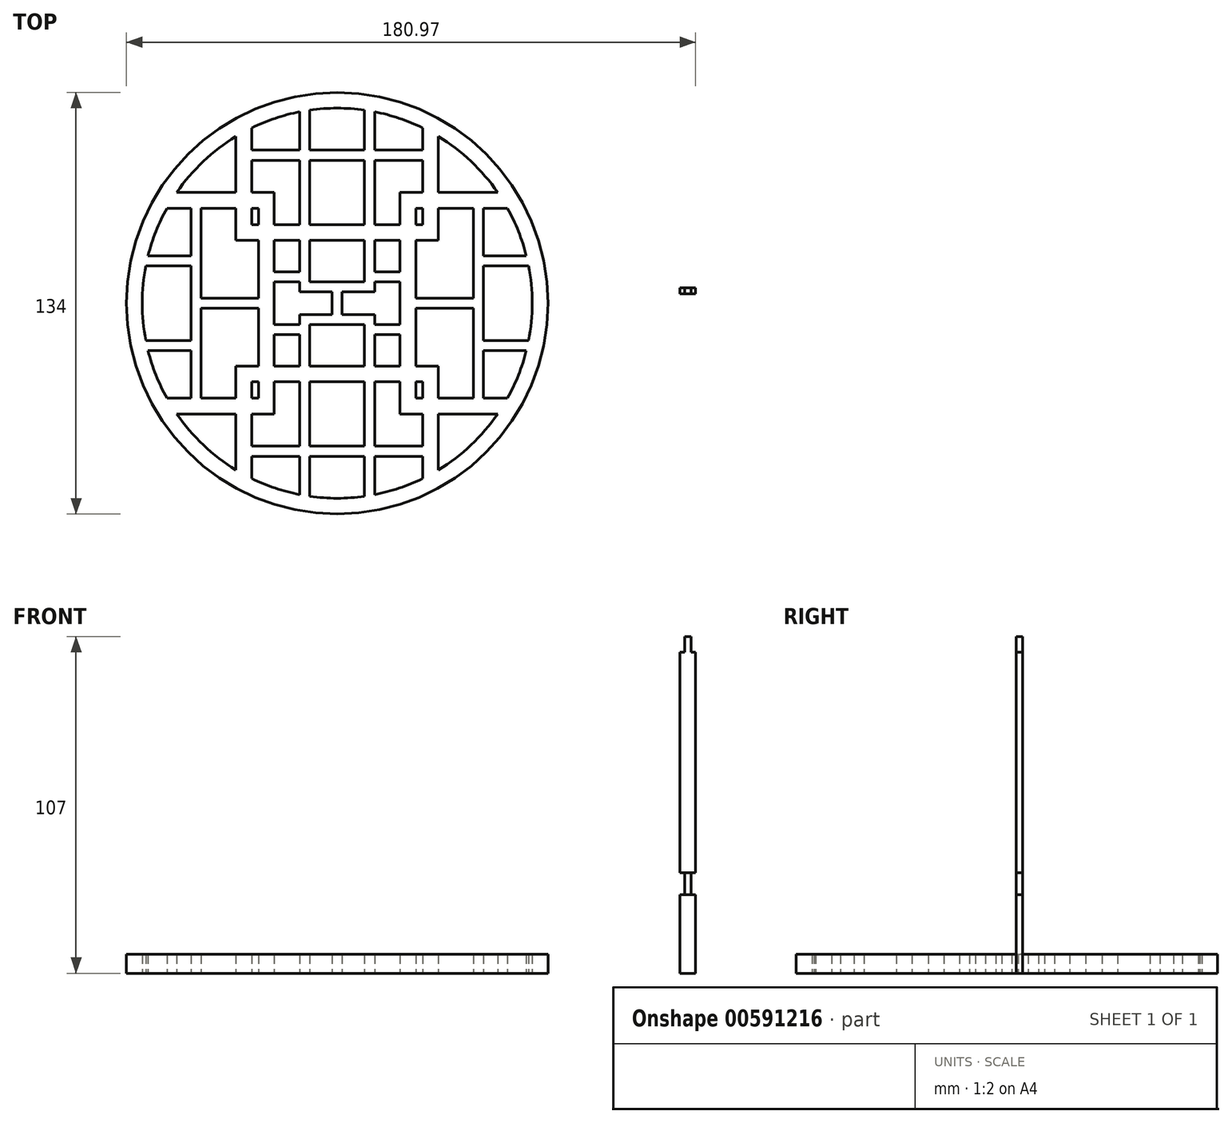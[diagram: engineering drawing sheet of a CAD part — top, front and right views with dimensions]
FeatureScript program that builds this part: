
annotation { "Feature Type Name" : "Feature", "Feature Type Description" : "" }
export const myFeature = defineFeature(function(context is Context, id is Id, definition is map)
    precondition{}
    {
        {
            var Q0;
            Q0=qCreatedBy(makeId("Top.planeOp"),FACE);
            var sketch = newSketch(context, id + "F0", { "sketchPlane" : qUnion([Q0])});
            skCircle(sketch, "E0", {"center": v(0, 0) * mm, "radius": 67 * mm});
            skArc(sketch, "E1.0", {"start": v(-54.15, 30.2) * mm, "mid": v(-57.64, 22.85) * mm, "end": v(-60.13, 15.1) * mm});
            skLineSegment(sketch, "E2.bottom", {"start": v(-27.2, 30.2) * mm, "end": v(-25, 30.2) * mm});
            skLineSegment(sketch, "E2.top", {"start": v(-27.2, 25) * mm, "end": v(-25, 25) * mm});
            skLineSegment(sketch, "E2.left", {"start": v(-27.2, 30.2) * mm, "end": v(-27.2, 25) * mm});
            skLineSegment(sketch, "E2.right", {"start": v(-25, 30.2) * mm, "end": v(-25, 25) * mm});
            skLineSegment(sketch, "E3.0", {"start": v(-20, 35.2) * mm, "end": v(-20, 25) * mm});
            skLineSegment(sketch, "E3.1", {"start": v(-27.2, 35.2) * mm, "end": v(-20, 35.2) * mm});
            skLineSegment(sketch, "E3.2", {"start": v(-32.2, 30.2) * mm, "end": v(-32.2, 20) * mm});
            skLineSegment(sketch, "E3.3", {"start": v(-32.2, 20) * mm, "end": v(-25, 20) * mm});
            skLineSegment(sketch, "E4", {"start": v(0, 62) * mm, "end": v(0, -62) * mm, "construction": true});
            skLineSegment(sketch, "E5", {"start": v(62, 0) * mm, "end": v(-62, 0) * mm, "construction": true});
            skLineSegment(sketch, "E6.0.1.0", {"start": v(-20, -25) * mm, "end": v(-20, -35.2) * mm});
            skLineSegment(sketch, "E6.0.1.1", {"start": v(-32.2, -20) * mm, "end": v(-32.2, -30.2) * mm});
            skLineSegment(sketch, "E6.0.1.2", {"start": v(-27.2, -35.2) * mm, "end": v(-20, -35.2) * mm});
            skLineSegment(sketch, "E6.0.1.3", {"start": v(-27.2, -30.2) * mm, "end": v(-25, -30.2) * mm});
            skLineSegment(sketch, "E6.0.1.4", {"start": v(-25, -25) * mm, "end": v(-25, -30.2) * mm});
            skLineSegment(sketch, "E6.0.1.5", {"start": v(-27.2, -25) * mm, "end": v(-27.2, -30.2) * mm});
            skLineSegment(sketch, "E6.0.1.6", {"start": v(-27.2, -25) * mm, "end": v(-25, -25) * mm});
            skLineSegment(sketch, "E6.0.1.7", {"start": v(-32.2, -20) * mm, "end": v(-25, -20) * mm});
            skLineSegment(sketch, "E6.1.0.0", {"start": v(32.2, 30.2) * mm, "end": v(32.2, 20) * mm});
            skLineSegment(sketch, "E6.1.0.1", {"start": v(20, 35.2) * mm, "end": v(20, 25) * mm});
            skLineSegment(sketch, "E6.1.0.2", {"start": v(25, 20) * mm, "end": v(32.2, 20) * mm});
            skLineSegment(sketch, "E6.1.0.3", {"start": v(25, 25) * mm, "end": v(27.2, 25) * mm});
            skLineSegment(sketch, "E6.1.0.4", {"start": v(27.2, 30.2) * mm, "end": v(27.2, 25) * mm});
            skLineSegment(sketch, "E6.1.0.5", {"start": v(25, 30.2) * mm, "end": v(25, 25) * mm});
            skLineSegment(sketch, "E6.1.0.6", {"start": v(25, 30.2) * mm, "end": v(27.2, 30.2) * mm});
            skLineSegment(sketch, "E6.1.0.7", {"start": v(20, 35.2) * mm, "end": v(27.2, 35.2) * mm});
            skLineSegment(sketch, "E6.1.1.0", {"start": v(32.2, -20) * mm, "end": v(32.2, -30.2) * mm});
            skLineSegment(sketch, "E6.1.1.1", {"start": v(20, -25) * mm, "end": v(20, -35.2) * mm});
            skLineSegment(sketch, "E6.1.1.2", {"start": v(20, -35.2) * mm, "end": v(27.2, -35.2) * mm});
            skLineSegment(sketch, "E6.1.1.3", {"start": v(25, -30.2) * mm, "end": v(27.2, -30.2) * mm});
            skLineSegment(sketch, "E6.1.1.4", {"start": v(27.2, -25) * mm, "end": v(27.2, -30.2) * mm});
            skLineSegment(sketch, "E6.1.1.5", {"start": v(25, -25) * mm, "end": v(25, -30.2) * mm});
            skLineSegment(sketch, "E6.1.1.6", {"start": v(25, -25) * mm, "end": v(27.2, -25) * mm});
            skLineSegment(sketch, "E6.1.1.7", {"start": v(25, -20) * mm, "end": v(32.2, -20) * mm});
            skLineSegment(sketch, "E6.direction1", {"start": v(-20, 20) * mm, "end": v(-11.9, 20) * mm, "construction": true});
            skLineSegment(sketch, "E6.direction2", {"start": v(-20, 20) * mm, "end": v(-20, 10) * mm, "construction": true});
            skLineSegment(sketch, "E7", {"start": v(-20, 20) * mm, "end": v(-20, 10) * mm});
            skLineSegment(sketch, "E8", {"start": v(-20, -20) * mm, "end": v(-11.9, -20) * mm});
            skLineSegment(sketch, "E9", {"start": v(20, 20) * mm, "end": v(20, 10) * mm});
            skLineSegment(sketch, "E10", {"start": v(20, 20) * mm, "end": v(11.9, 20) * mm});
            skLineSegment(sketch, "E11", {"start": v(25, 20) * mm, "end": v(25, 1.6) * mm});
            skPoint(sketch, "E12.orphan", {"position": v(-27.2, 20) * mm});
            skLineSegment(sketch, "E13", {"start": v(-25, 20) * mm, "end": v(-25, 1.6) * mm});
            skPoint(sketch, "E13.startSnap0", {"position": v(-26.1, 20) * mm});
            skLineSegment(sketch, "E14", {"start": v(-20, -25) * mm, "end": v(-11.9, -25) * mm});
            skLineSegment(sketch, "E15", {"start": v(20, 25) * mm, "end": v(11.9, 25) * mm});
            skLineSegment(sketch, "E16", {"start": v(27.2, -35.2) * mm, "end": v(27.2, -45.46) * mm});
            skPoint(sketch, "E16.startSnap0", {"position": v(26.1, -35.2) * mm});
            skLineSegment(sketch, "E17", {"start": v(32.2, -35.2) * mm, "end": v(32.2, -52.98) * mm});
            skLineSegment(sketch, "E18", {"start": v(32.2, -30.2) * mm, "end": v(43.26, -30.2) * mm});
            skPoint(sketch, "E18.startSnap0", {"position": v(32.2, -27.6) * mm});
            skLineSegment(sketch, "E19", {"start": v(32.2, -35.2) * mm, "end": v(51.04, -35.2) * mm});
            skLineSegment(sketch, "E20", {"start": v(32.2, 30.2) * mm, "end": v(43.26, 30.2) * mm});
            skLineSegment(sketch, "E21", {"start": v(32.2, 35.2) * mm, "end": v(51.04, 35.2) * mm});
            skLineSegment(sketch, "E22", {"start": v(32.2, 35.2) * mm, "end": v(32.2, 52.98) * mm});
            skLineSegment(sketch, "E23", {"start": v(27.2, 35.2) * mm, "end": v(27.2, 45.46) * mm});
            skLineSegment(sketch, "E24", {"start": v(-27.2, 35.2) * mm, "end": v(-27.2, 55.71) * mm});
            skLineSegment(sketch, "E25", {"start": v(-32.2, 35.2) * mm, "end": v(-32.2, 52.98) * mm});
            skLineSegment(sketch, "E26", {"start": v(-32.2, 35.2) * mm, "end": v(-51.04, 35.2) * mm});
            skLineSegment(sketch, "E27", {"start": v(-32.2, 30.2) * mm, "end": v(-43.26, 30.2) * mm});
            skLineSegment(sketch, "E28", {"start": v(-27.2, -35.2) * mm, "end": v(-27.2, -45.46) * mm});
            skPoint(sketch, "E28.startSnap0", {"position": v(-26.1, -35.2) * mm});
            skLineSegment(sketch, "E29", {"start": v(-32.2, -35.2) * mm, "end": v(-32.2, -52.98) * mm});
            skLineSegment(sketch, "E30", {"start": v(-32.2, -35.2) * mm, "end": v(-51.04, -35.2) * mm});
            skLineSegment(sketch, "E31", {"start": v(-32.2, -30.2) * mm, "end": v(-43.26, -30.2) * mm});
            skLineSegment(sketch, "E32", {"start": v(-11.9, -20) * mm, "end": v(-11.9, -10) * mm});
            skLineSegment(sketch, "E33.0", {"start": v(-8.7, -20) * mm, "end": v(-8.7, -6.8) * mm});
            skLineSegment(sketch, "E34", {"start": v(-11.9, -10) * mm, "end": v(-20, -10) * mm});
            skLineSegment(sketch, "E35", {"start": v(-11.9, -6.8) * mm, "end": v(-20, -6.8) * mm});
            skPoint(sketch, "E36.orphan", {"position": v(-11.9, 0) * mm});
            skLineSegment(sketch, "E37.trimOffspring", {"start": v(-20, -10) * mm, "end": v(-20, -20) * mm, "construction": true});
            skLineSegment(sketch, "E38.trimOffspring", {"start": v(-8.7, -20) * mm, "end": v(8.7, -20) * mm});
            skLineSegment(sketch, "E39.trimOffspring", {"start": v(-20, -25) * mm, "end": v(-20, -35.2) * mm, "construction": true});
            skLineSegment(sketch, "E40", {"start": v(-8.7, -6.8) * mm, "end": v(0, -6.8) * mm});
            skLineSegment(sketch, "E41", {"start": v(-1.6, -3.6) * mm, "end": v(-11.92, -3.6) * mm});
            skLineSegment(sketch, "E42", {"start": v(-11.92, -3.6) * mm, "end": v(-11.9, -6.8) * mm});
            skLineSegment(sketch, "E43", {"start": v(-1.6, -3.6) * mm, "end": v(-1.6, 0) * mm});
            skLineSegment(sketch, "E44.MirrorCS", {"start": v(8.7, -6.8) * mm, "end": v(0, -6.8) * mm});
            skLineSegment(sketch, "E45.MirrorCS", {"start": v(8.7, -20) * mm, "end": v(8.7, -6.8) * mm});
            skLineSegment(sketch, "E46.MirrorCS", {"start": v(11.9, -20) * mm, "end": v(11.9, -10) * mm});
            skLineSegment(sketch, "E47.MirrorCS", {"start": v(11.9, -10) * mm, "end": v(20, -10) * mm});
            skLineSegment(sketch, "E48.MirrorCS", {"start": v(11.9, -6.8) * mm, "end": v(20, -6.8) * mm});
            skLineSegment(sketch, "E49.MirrorCS", {"start": v(1.6, -3.6) * mm, "end": v(11.92, -3.6) * mm});
            skLineSegment(sketch, "E50.MirrorCS", {"start": v(1.6, -3.6) * mm, "end": v(1.6, 0) * mm});
            skLineSegment(sketch, "E51", {"start": v(11.92, -3.6) * mm, "end": v(11.9, -6.8) * mm});
            skLineSegment(sketch, "E52.MirrorCS", {"start": v(11.9, 10) * mm, "end": v(20, 10) * mm});
            skLineSegment(sketch, "E53.MirrorCS", {"start": v(11.9, 6.8) * mm, "end": v(20, 6.8) * mm});
            skLineSegment(sketch, "E54.MirrorCS", {"start": v(11.92, 3.6) * mm, "end": v(11.9, 6.8) * mm});
            skLineSegment(sketch, "E55.MirrorCS", {"start": v(1.6, 3.6) * mm, "end": v(11.92, 3.6) * mm});
            skLineSegment(sketch, "E56.MirrorCS", {"start": v(1.6, 3.6) * mm, "end": v(1.6, 0) * mm});
            skLineSegment(sketch, "E57.MirrorCS", {"start": v(-1.6, 3.6) * mm, "end": v(-1.6, 0) * mm});
            skLineSegment(sketch, "E58.MirrorCS", {"start": v(-8.7, 6.8) * mm, "end": v(0, 6.8) * mm});
            skLineSegment(sketch, "E59.MirrorCS", {"start": v(8.7, 6.8) * mm, "end": v(0, 6.8) * mm});
            skLineSegment(sketch, "E60.MirrorCS", {"start": v(8.7, 20) * mm, "end": v(8.7, 6.8) * mm});
            skLineSegment(sketch, "E61.MirrorCS", {"start": v(11.9, 20) * mm, "end": v(11.9, 10) * mm});
            skLineSegment(sketch, "E62.MirrorCS", {"start": v(-1.6, 3.6) * mm, "end": v(-11.92, 3.6) * mm});
            skLineSegment(sketch, "E63.MirrorCS", {"start": v(-8.7, 20) * mm, "end": v(-8.7, 6.8) * mm});
            skLineSegment(sketch, "E64.MirrorCS", {"start": v(-11.9, 20) * mm, "end": v(-11.9, 10) * mm});
            skLineSegment(sketch, "E65.MirrorCS", {"start": v(-11.9, 10) * mm, "end": v(-20, 10) * mm});
            skLineSegment(sketch, "E66.MirrorCS", {"start": v(-11.9, 6.8) * mm, "end": v(-20, 6.8) * mm});
            skLineSegment(sketch, "E67.MirrorCS", {"start": v(-11.92, 3.6) * mm, "end": v(-11.9, 6.8) * mm});
            skLineSegment(sketch, "E68.trimOffspring", {"start": v(-8.7, 20) * mm, "end": v(8.7, 20) * mm, "construction": true});
            skLineSegment(sketch, "E69.trimOffspring", {"start": v(-20, 6.8) * mm, "end": v(-20, -6.8) * mm, "construction": true});
            skLineSegment(sketch, "E70.trimOffspring", {"start": v(-20, 6.8) * mm, "end": v(-20, -6.8) * mm});
            skLineSegment(sketch, "E71.trimOffspring", {"start": v(-11.9, 20) * mm, "end": v(-20, 20) * mm});
            skLineSegment(sketch, "E72.trimOffspring", {"start": v(-20, -10) * mm, "end": v(-20, -20) * mm});
            skLineSegment(sketch, "E73.trimOffspring", {"start": v(11.9, -20) * mm, "end": v(20, -20) * mm});
            skLineSegment(sketch, "E74.trimOffspring", {"start": v(20, -10) * mm, "end": v(20, -20) * mm});
            skLineSegment(sketch, "E75.trimOffspring", {"start": v(20, 6.8) * mm, "end": v(20, -6.8) * mm});
            skLineSegment(sketch, "E76.trimOffspring", {"start": v(25, 20) * mm, "end": v(32.2, 20) * mm, "construction": true});
            skLineSegment(sketch, "E77.trimOffspring", {"start": v(11.9, 20) * mm, "end": v(20, 20) * mm, "construction": true});
            skLineSegment(sketch, "E78.trimOffspring", {"start": v(8.7, 20) * mm, "end": v(-8.7, 20) * mm});
            skArc(sketch, "E79.trimOffspring", {"start": v(-32.2, 52.98) * mm, "mid": v(-42.56, 45.09) * mm, "end": v(-51.04, 35.2) * mm});
            skArc(sketch, "E80.trimOffspring", {"start": v(27.2, 55.71) * mm, "mid": v(19.72, 58.78) * mm, "end": v(11.9, 60.85) * mm});
            skArc(sketch, "E81.trimOffspring", {"start": v(51.04, 35.2) * mm, "mid": v(42.56, 45.09) * mm, "end": v(32.2, 52.98) * mm});
            skArc(sketch, "E82.trimOffspring", {"start": v(54.15, -30.2) * mm, "mid": v(57.64, -22.85) * mm, "end": v(60.13, -15.1) * mm});
            skArc(sketch, "E83.trimOffspring", {"start": v(32.2, -52.98) * mm, "mid": v(42.56, -45.09) * mm, "end": v(51.04, -35.2) * mm});
            skArc(sketch, "E84.trimOffspring", {"start": v(-27.2, -55.71) * mm, "mid": v(-19.72, -58.78) * mm, "end": v(-11.9, -60.85) * mm});
            skArc(sketch, "E85.trimOffspring", {"start": v(-51.04, -35.2) * mm, "mid": v(-42.56, -45.09) * mm, "end": v(-32.2, -52.98) * mm});
            skLineSegment(sketch, "E86", {"start": v(-46.46, -30.2) * mm, "end": v(-46.46, -15.1) * mm});
            skLineSegment(sketch, "E87", {"start": v(-43.26, -30.2) * mm, "end": v(-43.26, -1.6) * mm});
            skLineSegment(sketch, "E88", {"start": v(-43.26, -1.6) * mm, "end": v(-25, -1.6) * mm});
            skPoint(sketch, "E89.orphan", {"position": v(-43.26, 0) * mm});
            skLineSegment(sketch, "E90", {"start": v(-46.46, -15.1) * mm, "end": v(-60.13, -15.1) * mm});
            skLineSegment(sketch, "E91", {"start": v(-46.46, -11.9) * mm, "end": v(-60.85, -11.9) * mm});
            skLineSegment(sketch, "E92.trimOffspring", {"start": v(-46.46, -11.9) * mm, "end": v(-46.46, 0) * mm});
            skArc(sketch, "E93.trimOffspring", {"start": v(-60.13, -15.1) * mm, "mid": v(-57.64, -22.85) * mm, "end": v(-54.15, -30.2) * mm});
            skLineSegment(sketch, "E94.MirrorCS", {"start": v(-43.26, 1.6) * mm, "end": v(-25, 1.6) * mm});
            skLineSegment(sketch, "E95.MirrorCS", {"start": v(-43.26, 30.2) * mm, "end": v(-43.26, 1.6) * mm});
            skLineSegment(sketch, "E96.MirrorCS", {"start": v(-46.46, 30.2) * mm, "end": v(-46.46, 15.1) * mm});
            skLineSegment(sketch, "E97.MirrorCS", {"start": v(-46.46, 11.9) * mm, "end": v(-46.46, 0) * mm});
            skLineSegment(sketch, "E98.MirrorCS", {"start": v(-46.46, 11.9) * mm, "end": v(-60.85, 11.9) * mm});
            skLineSegment(sketch, "E99.MirrorCS", {"start": v(-46.46, 15.1) * mm, "end": v(-60.13, 15.1) * mm});
            skLineSegment(sketch, "E100.MirrorCS", {"start": v(43.26, -30.2) * mm, "end": v(43.26, -1.6) * mm});
            skLineSegment(sketch, "E101.MirrorCS", {"start": v(43.26, -1.6) * mm, "end": v(25, -1.6) * mm});
            skLineSegment(sketch, "E102.MirrorCS", {"start": v(43.26, 1.6) * mm, "end": v(25, 1.6) * mm});
            skLineSegment(sketch, "E103.MirrorCS", {"start": v(46.46, -30.2) * mm, "end": v(46.46, -15.1) * mm});
            skLineSegment(sketch, "E104.MirrorCS", {"start": v(46.46, -11.9) * mm, "end": v(60.85, -11.9) * mm});
            skLineSegment(sketch, "E105.MirrorCS", {"start": v(46.46, 11.9) * mm, "end": v(60.85, 11.9) * mm});
            skLineSegment(sketch, "E106.MirrorCS", {"start": v(46.46, 15.1) * mm, "end": v(60.13, 15.1) * mm});
            skLineSegment(sketch, "E107.MirrorCS", {"start": v(43.26, 30.2) * mm, "end": v(43.26, 1.6) * mm});
            skLineSegment(sketch, "E108.MirrorCS", {"start": v(46.46, -15.1) * mm, "end": v(60.13, -15.1) * mm});
            skLineSegment(sketch, "E109.MirrorCS", {"start": v(46.46, 11.9) * mm, "end": v(46.46, 0) * mm});
            skLineSegment(sketch, "E110.MirrorCS", {"start": v(46.46, -11.9) * mm, "end": v(46.46, 0) * mm});
            skLineSegment(sketch, "E111.MirrorCS", {"start": v(46.46, 30.2) * mm, "end": v(46.46, 15.1) * mm});
            skLineSegment(sketch, "E112.trimOffspring", {"start": v(46.46, -30.2) * mm, "end": v(54.15, -30.2) * mm});
            skArc(sketch, "E113.trimOffspring", {"start": v(60.85, -11.9) * mm, "mid": v(62, 0) * mm, "end": v(60.85, 11.9) * mm});
            skArc(sketch, "E114.trimOffspring", {"start": v(60.13, 15.1) * mm, "mid": v(57.64, 22.85) * mm, "end": v(54.15, 30.2) * mm});
            skLineSegment(sketch, "E115.trimOffspring", {"start": v(46.46, 30.2) * mm, "end": v(54.15, 30.2) * mm});
            skLineSegment(sketch, "E116.trimOffspring", {"start": v(25, -1.6) * mm, "end": v(25, -20) * mm});
            skLineSegment(sketch, "E117.trimOffspring", {"start": v(-25, -1.6) * mm, "end": v(-25, -20) * mm});
            skArc(sketch, "E118.trimOffspring", {"start": v(-60.85, 11.9) * mm, "mid": v(-62, 0) * mm, "end": v(-60.85, -11.9) * mm});
            skLineSegment(sketch, "E119.trimOffspring", {"start": v(-46.46, -30.2) * mm, "end": v(-54.15, -30.2) * mm});
            skLineSegment(sketch, "E120.trimOffspring", {"start": v(-46.46, 30.2) * mm, "end": v(-54.15, 30.2) * mm});
            skLineSegment(sketch, "E121", {"start": v(-27.2, -45.46) * mm, "end": v(-11.9, -45.46) * mm});
            skLineSegment(sketch, "E122", {"start": v(-8.7, -25) * mm, "end": v(-8.7, -45.46) * mm});
            skPoint(sketch, "E122.startSnap0", {"position": v(0, -25) * mm});
            skLineSegment(sketch, "E123", {"start": v(-11.9, -25) * mm, "end": v(-11.9, -45.46) * mm});
            skLineSegment(sketch, "E124", {"start": v(8.7, -25) * mm, "end": v(8.7, -45.46) * mm});
            skLineSegment(sketch, "E125", {"start": v(11.9, -25) * mm, "end": v(11.9, -45.46) * mm});
            skLineSegment(sketch, "E126.0", {"start": v(-27.2, -48.66) * mm, "end": v(-11.9, -48.66) * mm});
            skArc(sketch, "E127.trimOffspring", {"start": v(11.9, -60.85) * mm, "mid": v(19.72, -58.78) * mm, "end": v(27.2, -55.71) * mm});
            skArc(sketch, "E128.trimOffspring", {"start": v(-8.7, -61.39) * mm, "mid": v(0, -62) * mm, "end": v(8.7, -61.39) * mm});
            skLineSegment(sketch, "E129.trimOffspring", {"start": v(-27.2, -48.66) * mm, "end": v(-27.2, -55.71) * mm});
            skLineSegment(sketch, "E130.trimOffspring", {"start": v(27.2, -48.66) * mm, "end": v(27.2, -55.71) * mm});
            skLineSegment(sketch, "E131.trimOffspring", {"start": v(11.9, -48.66) * mm, "end": v(11.9, -60.85) * mm});
            skLineSegment(sketch, "E132.trimOffspring", {"start": v(8.7, -48.66) * mm, "end": v(8.7, -61.39) * mm});
            skLineSegment(sketch, "E133.trimOffspring", {"start": v(11.9, -45.46) * mm, "end": v(27.2, -45.46) * mm});
            skLineSegment(sketch, "E134.trimOffspring", {"start": v(11.9, -48.66) * mm, "end": v(27.2, -48.66) * mm});
            skLineSegment(sketch, "E135.trimOffspring", {"start": v(-8.7, -48.66) * mm, "end": v(-8.7, -61.39) * mm});
            skLineSegment(sketch, "E136.trimOffspring", {"start": v(-8.7, -48.66) * mm, "end": v(8.7, -48.66) * mm});
            skLineSegment(sketch, "E137.trimOffspring", {"start": v(-8.7, -45.46) * mm, "end": v(8.7, -45.46) * mm});
            skLineSegment(sketch, "E138.trimOffspring", {"start": v(-11.9, -48.66) * mm, "end": v(-11.9, -60.85) * mm});
            skLineSegment(sketch, "E139.trimOffspring", {"start": v(-8.7, -25) * mm, "end": v(8.7, -25) * mm});
            skLineSegment(sketch, "E140.trimOffspring", {"start": v(11.9, -25) * mm, "end": v(20, -25) * mm});
            skLineSegment(sketch, "E141.MirrorCS", {"start": v(11.9, 48.66) * mm, "end": v(11.9, 60.85) * mm});
            skLineSegment(sketch, "E142.MirrorCS", {"start": v(11.9, 48.66) * mm, "end": v(27.2, 48.66) * mm});
            skLineSegment(sketch, "E143.MirrorCS", {"start": v(11.9, 45.46) * mm, "end": v(27.2, 45.46) * mm});
            skLineSegment(sketch, "E144.MirrorCS", {"start": v(11.9, 25) * mm, "end": v(11.9, 45.46) * mm});
            skLineSegment(sketch, "E145.MirrorCS", {"start": v(8.7, 25) * mm, "end": v(8.7, 45.46) * mm});
            skLineSegment(sketch, "E146.MirrorCS", {"start": v(8.7, 48.66) * mm, "end": v(8.7, 61.39) * mm});
            skLineSegment(sketch, "E147.MirrorCS", {"start": v(-8.7, 48.66) * mm, "end": v(-8.7, 61.39) * mm});
            skLineSegment(sketch, "E148.MirrorCS", {"start": v(-8.7, 48.66) * mm, "end": v(8.7, 48.66) * mm});
            skLineSegment(sketch, "E149.MirrorCS", {"start": v(-8.7, 45.46) * mm, "end": v(8.7, 45.46) * mm});
            skLineSegment(sketch, "E150.MirrorCS", {"start": v(-8.7, 25) * mm, "end": v(-8.7, 45.46) * mm});
            skLineSegment(sketch, "E151.MirrorCS", {"start": v(-11.9, 25) * mm, "end": v(-11.9, 45.46) * mm});
            skLineSegment(sketch, "E152.MirrorCS", {"start": v(-27.2, 45.46) * mm, "end": v(-11.9, 45.46) * mm});
            skLineSegment(sketch, "E153.MirrorCS", {"start": v(-27.2, 48.66) * mm, "end": v(-11.9, 48.66) * mm});
            skLineSegment(sketch, "E154.MirrorCS", {"start": v(-11.9, 48.66) * mm, "end": v(-11.9, 60.85) * mm});
            skArc(sketch, "E155.trimOffspring", {"start": v(-11.9, 60.85) * mm, "mid": v(-19.72, 58.78) * mm, "end": v(-27.2, 55.71) * mm});
            skArc(sketch, "E156.trimOffspring", {"start": v(8.7, 61.39) * mm, "mid": v(0, 62) * mm, "end": v(-8.7, 61.39) * mm});
            skLineSegment(sketch, "E157.trimOffspring", {"start": v(-11.9, 25) * mm, "end": v(-20, 25) * mm});
            skLineSegment(sketch, "E158.trimOffspring", {"start": v(8.7, 25) * mm, "end": v(-8.7, 25) * mm});
            skLineSegment(sketch, "E159.trimOffspring", {"start": v(27.2, 48.66) * mm, "end": v(27.2, 55.71) * mm});
            skSolve(sketch);
        }
        {
            var Q0;
            Q0=makeQuery(id+"F0.imprint","IMPRINT",FACE,{"disambiguationData":[TD([[makeQuery(id+"F0.imprint","IMPRINT",EDGE,{"derivedFrom":sQuery(id+"F0.wireOp",EDGE,"E0")}),1.0]])]});
            extrude(context, id + "F1", {"entities" : qUnion([Q0]), "depth" : 6 * mm, "offsetDistance" : 25 * mm});
        }
        {
            var Q0;
            Q0=qCreatedBy(makeId("Top.planeOp"),FACE);
            var sketch = newSketch(context, id + "F2", { "sketchPlane" : qUnion([Q0])});
            skLineSegment(sketch, "E160.bottom", {"start": v(108.97, 4.93) * mm, "end": v(113.97, 4.93) * mm});
            skLineSegment(sketch, "E160.top", {"start": v(108.97, 2.93) * mm, "end": v(113.97, 2.93) * mm});
            skLineSegment(sketch, "E160.left", {"start": v(108.97, 4.93) * mm, "end": v(108.97, 2.93) * mm});
            skLineSegment(sketch, "E160.right", {"start": v(113.97, 4.93) * mm, "end": v(113.97, 2.93) * mm});
            skSolve(sketch);
        }
        {
            var Q0;
            Q0=makeQuery(id+"F2.imprint","IMPRINT",FACE,{"disambiguationData":[TD([[makeQuery(id+"F2.imprint","IMPRINT",EDGE,{"derivedFrom":sQuery(id+"F2.wireOp",EDGE,"E160.bottom")}),-1.0]])]});
            extrude(context, id + "F3", {"entities" : qUnion([Q0]), "depth" : 25 * mm, "offsetDistance" : 25 * mm});
        }
        {
            var Q0;
            Q0=makeQuery(id+"F3.opExtrude","CAP_FACE",FACE,{"disambiguationData":[OSD([sQuery(id+"F2.wireOp",EDGE,"E160.bottom"),sQuery(id+"F2.wireOp",EDGE,"E160.top"),sQuery(id+"F2.wireOp",EDGE,"E160.left"),sQuery(id+"F2.wireOp",EDGE,"E160.right")])],"isStart":false});
            var sketch = newSketch(context, id + "F4", { "sketchPlane" : qUnion([Q0])});
            skLineSegment(sketch, "E161.bottom", {"start": v(110.47, 4.93) * mm, "end": v(112.47, 4.93) * mm});
            skLineSegment(sketch, "E161.top", {"start": v(110.47, 2.93) * mm, "end": v(112.47, 2.93) * mm});
            skLineSegment(sketch, "E161.left", {"start": v(110.47, 4.93) * mm, "end": v(110.47, 2.93) * mm});
            skLineSegment(sketch, "E161.right", {"start": v(112.47, 4.93) * mm, "end": v(112.47, 2.93) * mm});
            skSolve(sketch);
        }
        {
            var Q0;
            Q0=makeQuery(id+"F4.imprint","IMPRINT",FACE,{"disambiguationData":[TD([[makeQuery(id+"F4.imprint","IMPRINT",EDGE,{"derivedFrom":sQuery(id+"F4.wireOp",EDGE,"E161.bottom")}),-1.0]])]});
            extrude(context, id + "F5", {"entities" : qUnion([Q0]), "operationType" : NewBodyOperationType.ADD, "depth" : 7 * mm, "offsetDistance" : 25 * mm});
        }
        {
            var Q0;
            Q0=makeQuery(id+"F5.opExtrude","CAP_FACE",FACE,{"disambiguationData":[OSD([sQuery(id+"F4.wireOp",EDGE,"E161.bottom"),sQuery(id+"F4.wireOp",EDGE,"E161.top"),sQuery(id+"F4.wireOp",EDGE,"E161.left"),sQuery(id+"F4.wireOp",EDGE,"E161.right")])],"isStart":false});
            var sketch = newSketch(context, id + "F6", { "sketchPlane" : qUnion([Q0])});
            skLineSegment(sketch, "E162.bottom", {"start": v(108.97, 4.93) * mm, "end": v(113.97, 4.93) * mm});
            skLineSegment(sketch, "E162.top", {"start": v(108.97, 2.93) * mm, "end": v(113.97, 2.93) * mm});
            skLineSegment(sketch, "E162.left", {"start": v(108.97, 4.93) * mm, "end": v(108.97, 2.93) * mm});
            skLineSegment(sketch, "E162.right", {"start": v(113.97, 4.93) * mm, "end": v(113.97, 2.93) * mm});
            skSolve(sketch);
        }
        {
            var Q0;
            {var subQ2=sQuery(id+"F6.wireOp",EDGE,"E162.left");Q0=makeQuery(id+"F6.imprint","IMPRINT",FACE,{"disambiguationData":[TD([[makeQuery(id+"F6.imprint","IMPRINT",EDGE,{"derivedFrom":subQ2}),1.0]])]});}
            var Q1;
            {var subQ1=makeQuery(id+"F5.opExtrude","CAP_EDGE",EDGE,{"disambiguationData":[OSD([sQuery(id+"F4.wireOp",EDGE,"E161.left")])],"isStart":false});Q1=makeQuery(id+"F6.imprint","IMPRINT",FACE,{"disambiguationData":[TD([[makeQuery(id+"F6.imprint","IMPRINT",EDGE,{"derivedFrom":subQ1}),1.0]])]});}
            var Q2;
            {var subQ2=sQuery(id+"F6.wireOp",EDGE,"E162.right");Q2=makeQuery(id+"F6.imprint","IMPRINT",FACE,{"disambiguationData":[TD([[makeQuery(id+"F6.imprint","IMPRINT",EDGE,{"derivedFrom":subQ2}),-1.0]])]});}
            extrude(context, id + "F7", {"entities" : qUnion([Q0, Q1, Q2]), "operationType" : NewBodyOperationType.ADD, "depth" : 70 * mm, "offsetDistance" : 25 * mm});
        }
        {
            var Q0;
            Q0=makeQuery(id+"F7.opExtrude","CAP_FACE",FACE,{"disambiguationData":[OSD([sQuery(id+"F6.wireOp",EDGE,"E162.bottom"),sQuery(id+"F6.wireOp",EDGE,"E162.top"),sQuery(id+"F6.wireOp",EDGE,"E162.left"),sQuery(id+"F6.wireOp",EDGE,"E162.right")])],"isStart":false});
            var sketch = newSketch(context, id + "F8", { "sketchPlane" : qUnion([Q0])});
            skLineSegment(sketch, "E163.bottom", {"start": v(110.47, 4.93) * mm, "end": v(112.47, 4.93) * mm});
            skLineSegment(sketch, "E163.top", {"start": v(110.47, 2.93) * mm, "end": v(112.47, 2.93) * mm});
            skLineSegment(sketch, "E163.left", {"start": v(110.47, 4.93) * mm, "end": v(110.47, 2.93) * mm});
            skLineSegment(sketch, "E163.right", {"start": v(112.47, 4.93) * mm, "end": v(112.47, 2.93) * mm});
            skSolve(sketch);
        }
        {
            var Q0;
            Q0=makeQuery(id+"F8.imprint","IMPRINT",FACE,{"disambiguationData":[TD([[makeQuery(id+"F8.imprint","IMPRINT",EDGE,{"derivedFrom":sQuery(id+"F8.wireOp",EDGE,"E163.bottom")}),-1.0]])]});
            extrude(context, id + "F9", {"entities" : qUnion([Q0]), "operationType" : NewBodyOperationType.ADD, "depth" : 5 * mm, "offsetDistance" : 25 * mm});
        }
        {
            var Q0;
            Q0=makeQuery(id+"F5.opExtrude","SWEPT_EDGE",EDGE,{"disambiguationData":[OSD([sQuery(id+"F2.wireOp",EDGE,"E160.bottom"),sQuery(id+"F4.wireOp",EDGE,"E161.bottom"),sQuery(id+"F4.wireOp",EDGE,"E161.left")])]});
            var Q1;
            Q1=makeQuery(id+"F5.opExtrude","SWEPT_EDGE",EDGE,{"disambiguationData":[OSD([sQuery(id+"F2.wireOp",EDGE,"E160.top"),sQuery(id+"F4.wireOp",EDGE,"E161.top"),sQuery(id+"F4.wireOp",EDGE,"E161.left")])]});
            var Q2;
            Q2=makeQuery(id+"F5.opExtrude","SWEPT_EDGE",EDGE,{"disambiguationData":[OSD([sQuery(id+"F2.wireOp",EDGE,"E160.top"),sQuery(id+"F4.wireOp",EDGE,"E161.top"),sQuery(id+"F4.wireOp",EDGE,"E161.right")])]});
            var Q3;
            Q3=makeQuery(id+"F5.opExtrude","SWEPT_EDGE",EDGE,{"disambiguationData":[OSD([sQuery(id+"F2.wireOp",EDGE,"E160.bottom"),sQuery(id+"F4.wireOp",EDGE,"E161.bottom"),sQuery(id+"F4.wireOp",EDGE,"E161.right")])]});
            fillet(context, id + "F10", {"entities" : qUnion([Q0, Q1, Q2, Q3]), "radius" : 1 * mm, "tangentPropagation" : true, "allowEdgeOverflow" : false});
        }
    });
